FCSTD DOCUMENT  (FreeCAD 1.0R39319 (Git))
Label: Assembly_pan-tilt_Innomaker
License: All rights reserved
LicenseURL: https://en.wikipedia.org/wiki/All_rights_reserved
objects: App::FeaturePython×4, App::Link×2, Assembly::JointGroup×1, Assembly::AssemblyObject×1
EXTERNAL_REF file=../Part/Print/Variants/pan-tilt_base.FCStd obj=Body
EXTERNAL_REF file=../Part/Print/Variants/pan-tilt_Innomaker-mount.FCStd obj=Body

FEATURE [App::Link] Body
  LinkedObject = -> <external ../Part/Print/Variants/pan-tilt_base.FCStd>#Body
FEATURE [App::FeaturePython] GroundedJoint  # Assembly grounded joint (typed FeaturePython)
  ObjectToGround = -> Body
FEATURE [App::Link] Body002
  LinkPlacement = pos=(6.6e-15,15.2977,41.483) rot=(-1,0,0;0.017453rad)
  LinkedObject = -> <external ../Part/Print/Variants/pan-tilt_Innomaker-mount.FCStd>#Body
  Placement = pos=(6.6e-15,15.2977,41.483) rot=(-1,0,0;0.017453rad)
FEATURE [App::FeaturePython] Joint  label="Cylindrical"  # Assembly joint (typed FeaturePython)
  Activated = true
  AngleMax = 0
  AngleMin = 0
  Detach1 = false
  Detach2 = false
  Distance = 0
  Distance2 = 0
  EnableAngleMax = false
  EnableAngleMin = false
  EnableLengthMax = false
  EnableLengthMin = false
  JointType = 2 (Cylindrical)
  LengthMax = 0
  LengthMin = 0
  Placement1 = pos=(-26.735,-15.3,-7.1e-15) rot=(0.707107,0,0.707107;3.14159rad)
  Placement2 = pos=(-35,7.8e-15,41.75) rot=(0.57735,0.57735,0.57735;2.0944rad)
  Reference1 = -> Assembly [Body002.Face15,Body002.Face15]
  Reference2 = -> Assembly [Body.Face32,Body.Edge1]
FEATURE [App::FeaturePython] Joint001  label="Distance"  # Assembly joint (typed FeaturePython)
  Activated = true
  AngleMax = 0
  AngleMin = 0
  Detach1 = false
  Detach2 = false
  Distance = -0.5
  Distance2 = 0
  EnableAngleMax = false
  EnableAngleMin = false
  EnableLengthMax = false
  EnableLengthMin = false
  JointType = 5 (Distance)
  LengthMax = 0
  LengthMin = 0
  Placement1 = pos=(-25,1.63864,27.536) rot=(0,-1,0;1.5708rad)
  Placement2 = pos=(-24.5,-4.1529,-7.1e-15) rot=(0.57735,-0.57735,0.57735;4.18879rad)
  Reference1 = -> Assembly [Body.Face11,Body.Vertex48]
  Reference2 = -> Assembly [Body002.Face8,Body002.Vertex17]
FEATURE [App::FeaturePython] Joint002  label="Angle"  # Assembly joint (typed FeaturePython)
  Activated = true
  AngleMax = 0
  AngleMin = 0
  Detach1 = false
  Detach2 = false
  Distance = 180
  Distance2 = 0
  EnableAngleMax = false
  EnableAngleMin = false
  EnableLengthMax = false
  EnableLengthMin = false
  JointType = 8 (Angle)
  LengthMax = 0
  LengthMin = 0
  Placement1 = pos=(-14.5,3,-10.5) rot=(-0.57735,0.57735,0.57735;2.0944rad)
  Placement2 = pos=(-30,-7,48.75) rot=(0.57735,-0.57735,0.57735;2.0944rad)
  Reference1 = -> Assembly [Body002.Face18,Body002.Vertex8]
  Reference2 = -> Assembly [Body.Face24,Body.Edge10]
FEATURE [Assembly::JointGroup] Joints
  Group = -> [GroundedJoint,Joint,Joint001,Joint002]
FEATURE [Assembly::AssemblyObject] Assembly
  Group = -> [Joints,Body,GroundedJoint,Body002,Joint,Joint001,Joint002]
  Origin = -> Origin
  Type = Assembly

RESOLVED EXTERNAL PARTS (link-assembly join: the EXTERNAL_REF files above that resolve inside this repo's crawl, each included once):
---- part ../Part/Print/Variants/pan-tilt_base.FCStd = doc fcstd_e3f5aacca5b6 ----
FCSTD DOCUMENT  (FreeCAD 1.0R39319 (Git))
Label: pan-tilt_base
License: All rights reserved
LicenseURL: https://en.wikipedia.org/wiki/All_rights_reserved
objects: Sketcher::SketchObject×6, PartDesign::Pocket×5, PartDesign::Pad×1, PartDesign::Mirrored×1, PartDesign::Body×1, App::Part×1
note: 33 computed .brp shape members not serialized (recipe doc carries the construction recipe); baked Part::Feature solids carry a one-line shape summary decoded from their .brp

FEATURE [Sketcher::SketchObject] Sketch
  ArcFitTolerance = 1e-06
  AttachmentSupport = -> [XZ_Plane001]
  FullyConstrained = true
  MakeInternals = false
  MapMode = 5
  Placement = pos=(0,0,0) rot=(1,0,0;1.5708rad)
  sketch-geometry (6):
    g0: LineSegment StartX=0 StartY=0 StartZ=0 EndX=0 EndY=3 EndZ=0
    g1: LineSegment StartX=0 StartY=3 StartZ=0 EndX=25 EndY=3 EndZ=0
    g2: LineSegment StartX=25 StartY=3 StartZ=0 EndX=25 EndY=54.75 EndZ=0
    g3: LineSegment StartX=25 StartY=54.75 StartZ=0 EndX=35 EndY=54.75 EndZ=0
    g4: LineSegment StartX=35 StartY=54.75 StartZ=0 EndX=35 EndY=0 EndZ=0
    g5: LineSegment StartX=35 StartY=0 StartZ=0 EndX=0 EndY=0 EndZ=0
  constraints (17):
    c: Coincident(g-1,g0)
    c: PointOnObject(g0,g-2)
    c: Coincident(g0,g1)
    c: Horizontal(g1)
    c: Coincident(g1,g2)
    c: Vertical(g2)
    c: Coincident(g2,g3)
    c: Horizontal(g3)
    c: Coincident(g3,g4)
    c: PointOnObject(g4,g-1)
    c: Vertical(g4)
    c: Coincident(g4,g5)
    c: Coincident(g5,g0)
    c: Distance(g2,g-2) = 25
    c: Distance(g4,g2) = 10
    c: Distance(g5,g1) = 3
    c: Distance(g5,g3) = 54.75
FEATURE [PartDesign::Pad] Pad
  Direction = (0,-1,2e-16)
  Length = 7
  Length2 = 10
  Placement = pos=(0,0,0) rot=(1,0,0;1.5708rad)
  Profile = -> Sketch
  ReferenceAxis = -> Sketch [N_Axis]
  Refine = true
  Suppressed = false
  Type = 4
FEATURE [Sketcher::SketchObject] Sketch003
  ArcFitTolerance = 1e-06
  AttachmentSupport = -> [YZ_Plane001]
  FullyConstrained = true
  MakeInternals = false
  MapMode = 5
  Placement = pos=(0,0,0) rot=(0.57735,0.57735,0.57735;2.0944rad)
  sketch-geometry (1):
    g0: Circle CenterX=0 CenterY=41.75 CenterZ=0 NormalX=0 NormalY=0 NormalZ=1 AngleXU=0 Radius=4
  constraints (3):
    c: PointOnObject(g0,g-2)
    c: Diameter(g0) = 8
    c: DistanceY(g-1,g0) = 41.75
FEATURE [PartDesign::Pocket] Pocket
  BaseFeature = -> Pad
  Direction = (-1,0,0)
  Length = 5
  Length2 = 5
  Placement = pos=(0,0,0) rot=(1,0,0;1.5708rad)
  Profile = -> Sketch003
  ReferenceAxis = -> Sketch003 [N_Axis]
  Refine = true
  Reversed = true
  Suppressed = false
  Type = 1
FEATURE [Sketcher::SketchObject] Sketch004
  ArcFitTolerance = 1e-06
  AttachmentSupport = -> [Pocket]
  ExternalGeometry = -> [Pocket]
  FullyConstrained = true
  MakeInternals = false
  MapMode = 5
  Placement = pos=(0,-7,1.5e-15) rot=(1,0,0;1.5708rad)
  sketch-geometry (2):
    g0: GeomPoint X=30 Y=48.75 Z=0
    g1: Circle CenterX=30 CenterY=48.75 CenterZ=0 NormalX=0 NormalY=0 NormalZ=1 AngleXU=0 Radius=3
  constraints (4):
    c: Distance(g0,g-1) = 48.75
    c: Distance(g0,g-3) = 5
    c: Coincident(g1,g0)
    c: Diameter(g1) = 6
FEATURE [PartDesign::Pocket] Pocket001
  BaseFeature = -> Pocket
  Direction = (0,1,-2e-16)
  Length = 5
  Length2 = 5
  Placement = pos=(0,0,0) rot=(1,0,0;1.5708rad)
  Profile = -> Sketch004
  ReferenceAxis = -> Sketch004 [N_Axis]
  Refine = true
  Suppressed = false
  Type = 1
FEATURE [Sketcher::SketchObject] Sketch006
  ArcFitTolerance = 1e-06
  FullyConstrained = true
  MakeInternals = false
  MapMode = 5
  Placement = pos=(0,10,-2.2e-15) rot=(-1,0,0;1.5708rad)
  sketch-geometry (8):
    g0: LineSegment StartX=30 StartY=-44 StartZ=0 EndX=25.8864 EndY=-46.375 EndZ=0
    g1: LineSegment StartX=25.8864 StartY=-46.375 StartZ=0 EndX=25.8864 EndY=-51.125 EndZ=0
    g2: LineSegment StartX=25.8864 StartY=-51.125 StartZ=0 EndX=30 EndY=-53.5 EndZ=0
    g3: LineSegment StartX=30 StartY=-53.5 StartZ=0 EndX=34.1136 EndY=-51.125 EndZ=0
    g4: LineSegment StartX=34.1136 StartY=-51.125 StartZ=0 EndX=34.1136 EndY=-46.375 EndZ=0
    g5: LineSegment StartX=34.1136 StartY=-46.375 StartZ=0 EndX=30 EndY=-44 EndZ=0
    g6: Circle [constr] CenterX=30 CenterY=-48.75 CenterZ=0 NormalX=0 NormalY=0 NormalZ=1 AngleXU=0 Radius=4.75
    g7: LineSegment [constr] StartX=30 StartY=-53.5 StartZ=0 EndX=30 EndY=-44 EndZ=0
  constraints (18):
    c: Coincident(g0,g1)
    c: Coincident(g1,g2)
    c: Coincident(g2,g3)
    c: Coincident(g3,g4)
    c: Coincident(g4,g5)
    c: Coincident(g5,g0)
    c: Equal(g0, g1-g5) x5
    c: PointOnObject(g0,g6)
    c: PointOnObject(g1,g6)
    c: PointOnObject(g2,g6)
    c: PointOnObject(g3,g6)
    c: PointOnObject(g4,g6)
    c: PointOnObject(g5,g6)
    c: Diameter(g6) = 9.5
    c: Coincident(g6,g-3)
    c: Coincident(g7,g2)
    c: Coincident(g7,g0)
    c: Vertical(g7)
FEATURE [PartDesign::Pocket] Pocket003
  BaseFeature = -> Pocket001
  Direction = (0,-1,-2e-16)
  Length = 5
  Length2 = 5
  Placement = pos=(0,0,0) rot=(1,0,0;1.5708rad)
  Profile = -> Sketch006
  ReferenceAxis = -> Sketch006 [N_Axis]
  Refine = true
  Suppressed = false
  Type = 0
FEATURE [Sketcher::SketchObject] Sketch007
  ArcFitTolerance = 1e-06
  AttachmentSupport = -> [YZ_Plane001]
  ExternalGeometry = -> [Pocket003]
  FullyConstrained = true
  MakeInternals = false
  MapMode = 5
  Placement = pos=(0,0,0) rot=(0.57735,0.57735,0.57735;2.0944rad)
  sketch-geometry (4):
    g0: LineSegment StartX=-1 StartY=54.75 StartZ=0 EndX=-1 EndY=34.75 EndZ=0
    g1: LineSegment StartX=-1 StartY=34.75 StartZ=0 EndX=1 EndY=34.75 EndZ=0
    g2: LineSegment StartX=1 StartY=34.75 StartZ=0 EndX=1 EndY=54.75 EndZ=0
    g3: LineSegment StartX=1 StartY=54.75 StartZ=0 EndX=-1 EndY=54.75 EndZ=0
  constraints (11):
    c: Coincident(g0,g1)
    c: Coincident(g1,g2)
    c: Coincident(g2,g3)
    c: Coincident(g3,g0)
    c: Vertical(g0)
    c: Vertical(g2)
    c: Horizontal(g1)
    c: PointOnObject(g2,g-3)
    c: Symmetric(g0,g2,g-2)
    c: DistanceY(g2,g2) = 20
    c: Distance(g2,g0) = 2
FEATURE [PartDesign::Pocket] Pocket004
  BaseFeature = -> Pocket003
  Direction = (-1,0,0)
  Length = 5
  Length2 = 5
  Placement = pos=(0,0,0) rot=(1,0,0;1.5708rad)
  Profile = -> Sketch007
  ReferenceAxis = -> Sketch007 [N_Axis]
  Refine = true
  Reversed = true
  Suppressed = false
  Type = 1
FEATURE [PartDesign::Mirrored] Mirrored
  BaseFeature = -> Pocket004
  MirrorPlane = -> YZ_Plane001
  Placement = pos=(0,0,0) rot=(1,0,0;1.5708rad)
  Refine = true
  Suppressed = false
  TransformMode = 1
FEATURE [Sketcher::SketchObject] Sketch008
  ArcFitTolerance = 1e-06
  AttachmentSupport = -> [XY_Plane001]
  FullyConstrained = true
  MakeInternals = false
  MapMode = 5
  sketch-geometry (1):
    g0: Circle CenterX=0 CenterY=0 CenterZ=0 NormalX=0 NormalY=0 NormalZ=1 AngleXU=0 Radius=2.75
  constraints (2):
    c: Coincident(g0,g-1)
    c: Diameter(g0) = 5.5
FEATURE [PartDesign::Pocket] Pocket005
  BaseFeature = -> Mirrored
  Direction = (0,0,-1)
  Length = 5
  Length2 = 5
  Placement = pos=(0,0,0) rot=(1,0,0;1.5708rad)
  Profile = -> Sketch008
  ReferenceAxis = -> Sketch008 [N_Axis]
  Refine = true
  Reversed = true
  Suppressed = false
  Type = 1
FEATURE [PartDesign::Body] Body
  AllowCompound = false
  Group = -> [Sketch,Pad,Sketch003,Pocket,Sketch004,Pocket001,Sketch006,Pocket003,Sketch007,Pocket004,Mirrored,Sketch008,Pocket005]
  Origin = -> Origin001
  Tip = -> Pocket005
FEATURE [App::Part] Part
  Group = -> [Body]
  Origin = -> Origin
